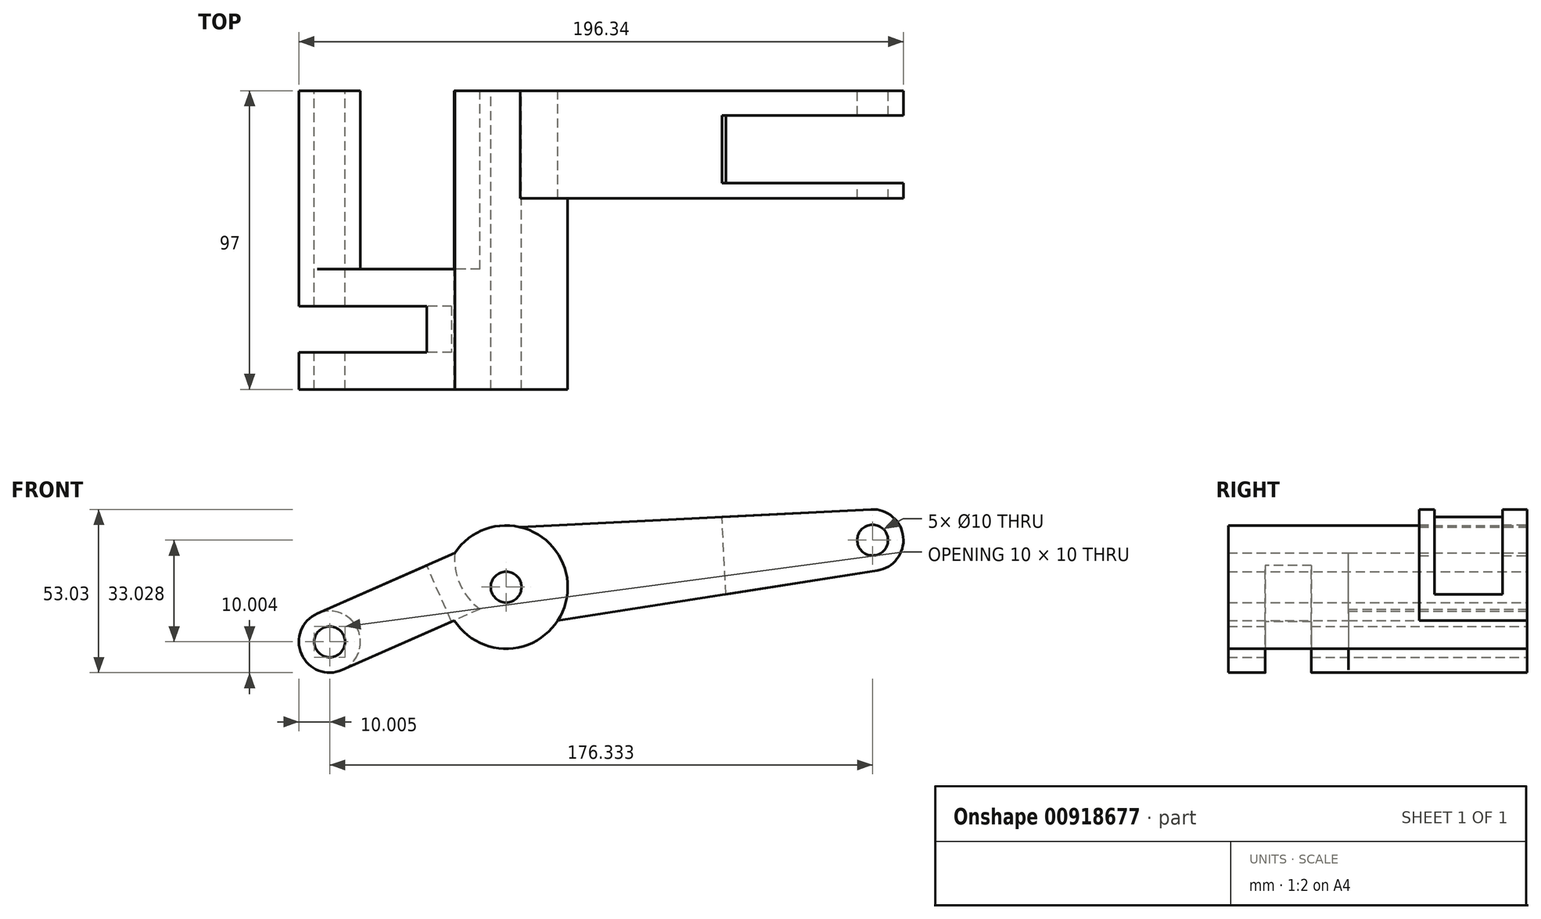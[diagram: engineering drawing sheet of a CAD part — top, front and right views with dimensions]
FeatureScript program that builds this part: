
annotation { "Feature Type Name" : "Feature", "Feature Type Description" : "" }
export const myFeature = defineFeature(function(context is Context, id is Id, definition is map)
    precondition{}
    {
        {
            var Q0;
            Q0=qCreatedBy(makeId("Front.planeOp"),FACE);
            var sketch = newSketch(context, id + "F0", { "sketchPlane" : qUnion([Q0])});
            skArc(sketch, "E0", {"start": v(-78.14, -23.6) * mm, "mid": v(-83.24, -36.8) * mm, "end": v(-70.05, -41.9) * mm});
            skCircle(sketch, "E1", {"center": v(-16.79, -14.98) * mm, "radius": 5 * mm});
            skCircle(sketch, "E2", {"center": v(-74.1, -32.76) * mm, "radius": 5 * mm});
            skLineSegment(sketch, "E3", {"start": v(-78.14, -23.6) * mm, "end": v(-33.4, -3.83) * mm});
            skLineSegment(sketch, "E4", {"start": v(-70.05, -41.9) * mm, "end": v(-33.61, -25.8) * mm});
            skArc(sketch, "E5", {"start": v(-33.61, -25.8) * mm, "mid": v(3.2, -15.18) * mm, "end": v(-33.4, -3.83) * mm});
            skCircle(sketch, "E6", {"center": v(102.24, 0.27) * mm, "radius": 5 * mm});
            skLineSegment(sketch, "E7", {"start": v(-12.25, 4.5) * mm, "end": v(101.73, 10.26) * mm});
            skCircle(sketch, "E8", {"center": v(102.24, 0.27) * mm, "radius": 10 * mm});
            skLineSegment(sketch, "E9", {"start": v(0, -25.85) * mm, "end": v(103.78, -9.6) * mm});
            skPoint(sketch, "E10.center.orphan", {"position": v(72.24, 31.94) * mm});
            skSolve(sketch);
        }
        {
            var Q0;
            Q0=makeQuery(id+"F0.imprint","IMPRINT",FACE,{"disambiguationData":[TD([[makeQuery(id+"F0.imprint","IMPRINT",EDGE,{"derivedFrom":sQuery(id+"F0.wireOp",EDGE,"E0")}),1.0]])]});
            extrude(context, id + "F1", {"entities" : qUnion([Q0]), "depth" : 97 * mm, "offsetDistance" : 25 * mm});
        }
        {
            var Q0;
            Q0 = qSketchRegion(id + "F0", true);
            extrude(context, id + "F2", {"entities" : qUnion([Q0]), "operationType" : NewBodyOperationType.ADD, "depth" : 35 * mm, "offsetDistance" : 25 * mm});
        }
        {
            var Q0;
            {var subQ0=sQuery(id+"F0.wireOp",EDGE,"E5");var subQ1=sQuery(id+"F0.wireOp",EDGE,"E4");var subQ2=sQuery(id+"F0.wireOp",EDGE,"E3");var subQ3=sQuery(id+"F0.wireOp",EDGE,"E2");var subQ4=sQuery(id+"F0.wireOp",EDGE,"E1");var subQ5=sQuery(id+"F0.wireOp",EDGE,"E0");Q0=makeQuery(id+"F2.boolean.opBoolean","MERGE",FACE,{"derivedFrom":[makeQuery(id+"F1.opExtrude","CAP_FACE",FACE,{"disambiguationData":[OSD([subQ5,subQ4,subQ3,subQ2,subQ1,subQ0])],"isStart":true}),makeQuery(id+"F2.opExtrude","CAP_FACE",FACE,{"disambiguationData":[OSD([subQ5,sQuery(id+"F0.wireOp",EDGE,"c24a90be-7e30-4a72-8988-e234462c8f6e"),subQ4,subQ3,sQuery(id+"F0.wireOp",EDGE,"E10"),subQ2,subQ1,subQ0,sQuery(id+"F0.wireOp",EDGE,"b02dfb3e-fab2-4523-9738-0b89780c768d.trimOffspring"),sQuery(id+"F0.wireOp",EDGE,"da3bd604-1aeb-43cc-881d-e09999a3ad17.trimOffspring")])],"isStart":true})]});}
            var sketch = newSketch(context, id + "F3", { "sketchPlane" : qUnion([Q0])});
            skArc(sketch, "E11", {"start": v(25.3, -22.12) * mm, "mid": v(31.8, -14.06) * mm, "end": v(33.4, -3.83) * mm});
            skCircle(sketch, "E12", {"center": v(74.1, -32.76) * mm, "radius": 10 * mm});
            skLineSegment(sketch, "E13", {"start": v(25.3, -22.12) * mm, "end": v(70.05, -41.9) * mm});
            skLineSegment(sketch, "E14", {"start": v(33.4, -3.83) * mm, "end": v(78.14, -23.6) * mm});
            skSolve(sketch);
        }
        {
            var Q0;
            Q0=makeQuery(id+"F3.imprint","IMPRINT",FACE,{"disambiguationData":[TD([[makeQuery(id+"F3.imprint","IMPRINT",EDGE,{"derivedFrom":sQuery(id+"F3.wireOp",EDGE,"E11")}),-1.0]])]});
            var Q1;
            {var subQ0=sQuery(id+"F3.wireOp",EDGE,"E12");Q1=makeQuery(id+"F3.imprint","IMPRINT",FACE,{"disambiguationData":[TD([[makeQuery(id+"F3.imprint","IMPRINT",EDGE,{"disambiguationData":[OD(0.0)],"derivedFrom":subQ0}),-1.0]])]});}
            extrude(context, id + "F4", {"entities" : qUnion([Q0, Q1]), "operationType" : NewBodyOperationType.REMOVE, "oppositeDirection" : true, "depth" : 58 * mm, "offsetDistance" : 25 * mm});
        }
        {
            var Q0;
            Q0=makeQuery(id+"F1.opExtrude","SWEPT_FACE",FACE,{"disambiguationData":[OSD([sQuery(id+"F0.wireOp",EDGE,"E3")])]});
            var sketch = newSketch(context, id + "F5", { "sketchPlane" : qUnion([Q0])});
            skLineSegment(sketch, "E15.bottom", {"start": v(-42.17, -70) * mm, "end": v(-102.17, -70) * mm});
            skLineSegment(sketch, "E15.top", {"start": v(-42.17, -85) * mm, "end": v(-102.17, -85) * mm});
            skLineSegment(sketch, "E15.left", {"start": v(-42.17, -70) * mm, "end": v(-42.17, -85) * mm});
            skLineSegment(sketch, "E15.right", {"start": v(-102.17, -70) * mm, "end": v(-102.17, -85) * mm});
            skSolve(sketch);
        }
        {
            var Q0;
            {var subQ0=sQuery(id+"F5.wireOp",EDGE,"E15.right");Q0=makeQuery(id+"F5.imprint","IMPRINT",FACE,{"disambiguationData":[TD([[makeQuery(id+"F5.imprint","IMPRINT",EDGE,{"derivedFrom":subQ0}),1.0]])]});}
            var Q1;
            {var subQ0=sQuery(id+"F5.wireOp",EDGE,"E15.left");Q1=makeQuery(id+"F5.imprint","IMPRINT",FACE,{"disambiguationData":[TD([[makeQuery(id+"F5.imprint","IMPRINT",EDGE,{"derivedFrom":subQ0}),-1.0]])]});}
            extrude(context, id + "F6", {"entities" : qUnion([Q0, Q1]), "operationType" : NewBodyOperationType.REMOVE, "endBound" : BoundingType.THROUGH_ALL, "oppositeDirection" : true, "depth" : 25 * mm, "offsetDistance" : 25 * mm});
        }
        {
            var Q0;
            Q0=makeQuery(id+"F2.opExtrude","SWEPT_FACE",FACE,{"disambiguationData":[OSD([sQuery(id+"F0.wireOp",EDGE,"E7")])]});
            var sketch = newSketch(context, id + "F7", { "sketchPlane" : qUnion([Q0])});
            skLineSegment(sketch, "E16.bottom", {"start": v(53.64, -8) * mm, "end": v(113.64, -8) * mm});
            skLineSegment(sketch, "E16.top", {"start": v(53.64, -30) * mm, "end": v(113.64, -30) * mm});
            skLineSegment(sketch, "E16.left", {"start": v(53.64, -8) * mm, "end": v(53.64, -30) * mm});
            skLineSegment(sketch, "E16.right", {"start": v(113.64, -8) * mm, "end": v(113.64, -30) * mm});
            skSolve(sketch);
        }
        {
            var Q0;
            {var subQ0=sQuery(id+"F7.wireOp",EDGE,"E16.left");Q0=makeQuery(id+"F7.imprint","IMPRINT",FACE,{"disambiguationData":[TD([[makeQuery(id+"F7.imprint","IMPRINT",EDGE,{"derivedFrom":subQ0}),1.0]])]});}
            var Q1;
            {var subQ0=sQuery(id+"F7.wireOp",EDGE,"E16.right");Q1=makeQuery(id+"F7.imprint","IMPRINT",FACE,{"disambiguationData":[TD([[makeQuery(id+"F7.imprint","IMPRINT",EDGE,{"derivedFrom":subQ0}),-1.0]])]});}
            extrude(context, id + "F8", {"entities" : qUnion([Q0, Q1]), "operationType" : NewBodyOperationType.REMOVE, "endBound" : BoundingType.THROUGH_ALL, "oppositeDirection" : true, "depth" : 25 * mm, "offsetDistance" : 25 * mm});
        }
    });
